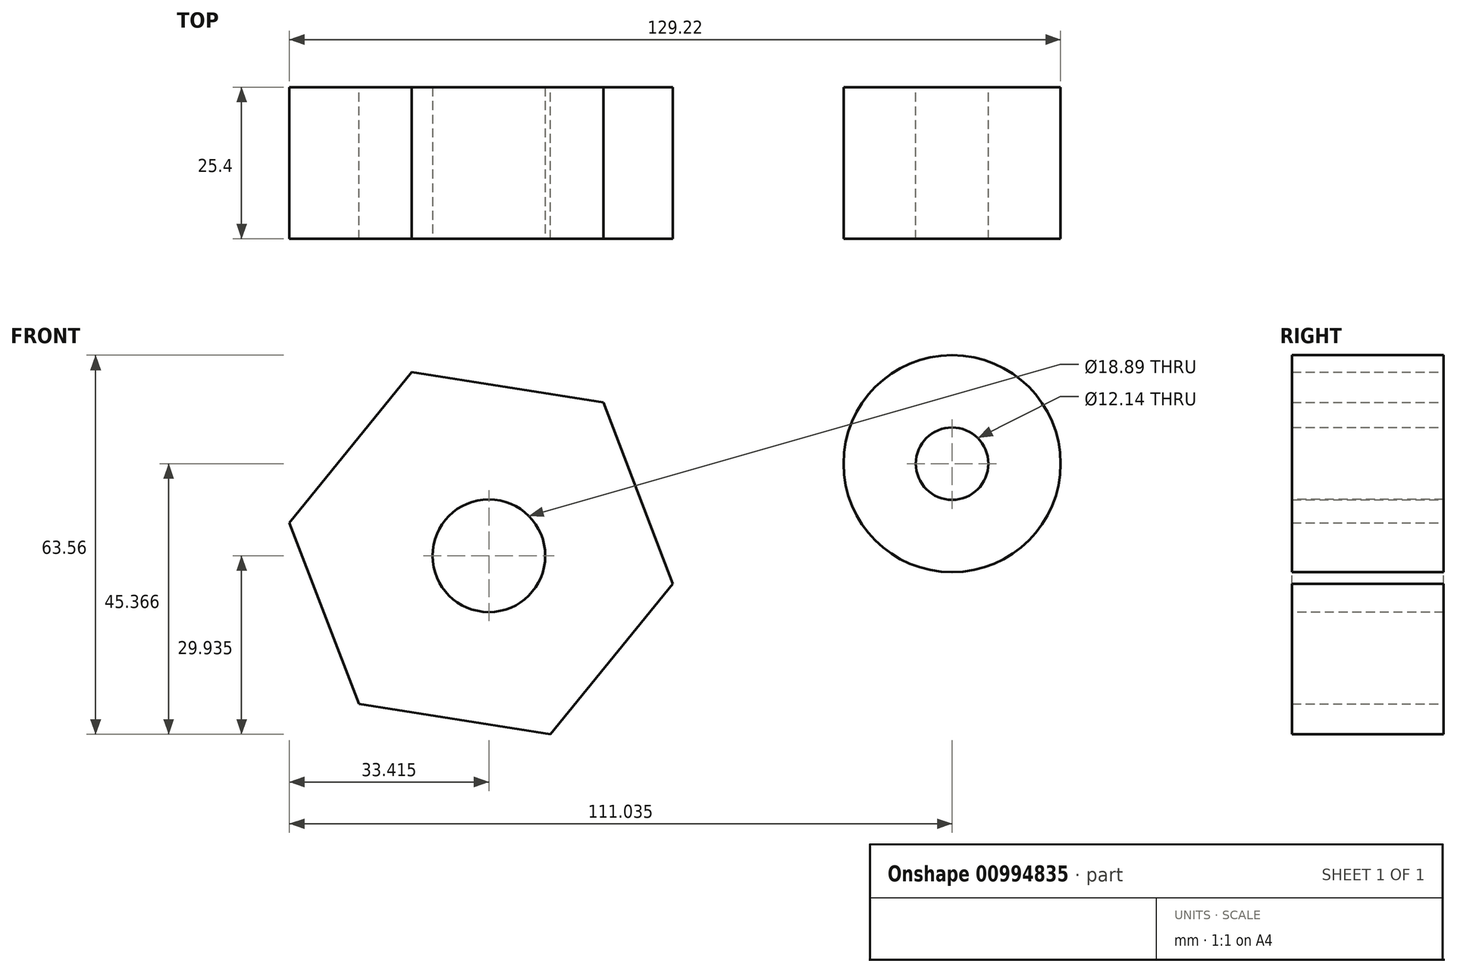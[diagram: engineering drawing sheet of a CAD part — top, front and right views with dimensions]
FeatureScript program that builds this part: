
annotation { "Feature Type Name" : "Feature", "Feature Type Description" : "" }
export const myFeature = defineFeature(function(context is Context, id is Id, definition is map)
    precondition{}
    {
        {
            var Q0;
            Q0=qCreatedBy(makeId("Front.planeOp"),FACE);
            var sketch = newSketch(context, id + "F0", { "sketchPlane" : qUnion([Q0])});
            skCircle(sketch, "E0", {"center": v(-46.4, -9.3) * mm, "radius": 16.6 * mm});
            skSolve(sketch);
        }
        {
            var Q0;
            Q0=qCreatedBy(makeId("Front.planeOp"),FACE);
            var sketch = newSketch(context, id + "F1", { "sketchPlane" : qUnion([Q0])});
            skCircle(sketch, "E1", {"center": v(46.81, -8.8) * mm, "radius": 18.19 * mm});
            skSolve(sketch);
        }
        {
            var Q0;
            Q0=makeQuery(id+"F0.imprint","IMPRINT",FACE,{"disambiguationData":[TD([[makeQuery(id+"F0.imprint","IMPRINT",EDGE,{"derivedFrom":sQuery(id+"F0.wireOp",EDGE,"E0")}),1.0]])]});
            extrude(context, id + "F2", {"entities" : qUnion([Q0]), "depth" : 25.4 * mm, "offsetDistance" : 25.4 * mm});
        }
        {
            var Q0;
            Q0=makeQuery(id+"F2.opExtrude","CAP_FACE",FACE,{"disambiguationData":[OSD([sQuery(id+"F0.wireOp",EDGE,"E0")])],"isStart":false});
            var sketch = newSketch(context, id + "F3", { "sketchPlane" : qUnion([Q0])});
            skCircle(sketch, "E2", {"center": v(-46.4, -9.3) * mm, "radius": 4.84 * mm});
            skSolve(sketch);
        }
        {
            var Q0;
            Q0 = qSketchRegion(id + "F3", true);
            var Q1;
            Q1=makeQuery(id+"F3.imprint","IMPRINT",FACE,{"disambiguationData":[TD([[makeQuery(id+"F3.imprint","IMPRINT",EDGE,{"derivedFrom":sQuery(id+"F3.wireOp",EDGE,"E2")}),1.0]])]});
            var Q2;
            Q2=makeQuery(id+"F3.imprint","IMPRINT",FACE,{"disambiguationData":[TD([[makeQuery(id+"F3.imprint","IMPRINT",EDGE,{"derivedFrom":sQuery(id+"F3.wireOp",EDGE,"E2")}),-1.0]])]});
            extrude(context, id + "F4", {"entities" : qUnion([Q0, Q1, Q2]), "operationType" : NewBodyOperationType.REMOVE, "oppositeDirection" : true, "depth" : 25.4 * mm, "offsetDistance" : 25.4 * mm});
        }
        {
            var Q0;
            Q0=makeQuery(id+"F1.imprint","IMPRINT",FACE,{"disambiguationData":[TD([[makeQuery(id+"F1.imprint","IMPRINT",EDGE,{"derivedFrom":sQuery(id+"F1.wireOp",EDGE,"E1")}),1.0]])]});
            extrude(context, id + "F5", {"entities" : qUnion([Q0]), "depth" : 25.4 * mm, "offsetDistance" : 25.4 * mm});
        }
        {
            var Q0;
            Q0=makeQuery(id+"F5.opExtrude","CAP_FACE",FACE,{"disambiguationData":[OSD([sQuery(id+"F1.wireOp",EDGE,"E1")])],"isStart":true});
            var sketch = newSketch(context, id + "F6", { "sketchPlane" : qUnion([Q0])});
            skCircle(sketch, "E3", {"center": v(-46.81, -8.8) * mm, "radius": 6.07 * mm});
            skSolve(sketch);
        }
        {
            var Q0;
            Q0=makeQuery(id+"F6.imprint","IMPRINT",FACE,{"disambiguationData":[TD([[makeQuery(id+"F6.imprint","IMPRINT",EDGE,{"derivedFrom":sQuery(id+"F6.wireOp",EDGE,"E3")}),1.0]])]});
            extrude(context, id + "F7", {"entities" : qUnion([Q0]), "operationType" : NewBodyOperationType.REMOVE, "oppositeDirection" : true, "depth" : 27.23 * mm, "offsetDistance" : 25.4 * mm});
        }
        {
            var Q0;
            Q0=qCreatedBy(makeId("Front.planeOp"),FACE);
            var sketch = newSketch(context, id + "F8", { "sketchPlane" : qUnion([Q0])});
            skCircle(sketch, "E4.cCircle", {"center": v(-32.11, -23.8) * mm, "radius": 32.51 * mm, "construction": true});
            skLineSegment(sketch, "E4.0", {"start": v(0, -28.91) * mm, "end": v(-20.48, -54.16) * mm});
            skLineSegment(sketch, "E4.1", {"start": v(-20.48, -54.16) * mm, "end": v(-52.6, -49.05) * mm});
            skLineSegment(sketch, "E4.2", {"start": v(-52.6, -49.05) * mm, "end": v(-64.22, -18.7) * mm});
            skLineSegment(sketch, "E4.3", {"start": v(-64.22, -18.7) * mm, "end": v(-43.74, 6.56) * mm});
            skLineSegment(sketch, "E4.4", {"start": v(-43.74, 6.56) * mm, "end": v(-11.63, 1.45) * mm});
            skLineSegment(sketch, "E4.5", {"start": v(-11.63, 1.45) * mm, "end": v(0, -28.91) * mm});
            skSolve(sketch);
        }
        {
            var Q0;
            Q0 = qSketchRegion(id + "F8", true);
            var Q1;
            Q1=makeQuery(id+"F8.imprint","IMPRINT",FACE,{"disambiguationData":[TD([[makeQuery(id+"F8.imprint","IMPRINT",EDGE,{"derivedFrom":sQuery(id+"F8.wireOp",EDGE,"E4.0")}),-1.0]])]});
            extrude(context, id + "F9", {"entities" : qUnion([Q0, Q1]), "depth" : 25.4 * mm, "offsetDistance" : 25.4 * mm});
        }
        {
            var Q0;
            Q0=makeQuery(id+"F9.opExtrude","CAP_FACE",FACE,{"disambiguationData":[OSD([sQuery(id+"F8.wireOp",EDGE,"E4.0"),sQuery(id+"F8.wireOp",EDGE,"E4.1"),sQuery(id+"F8.wireOp",EDGE,"E4.2"),sQuery(id+"F8.wireOp",EDGE,"E4.3"),sQuery(id+"F8.wireOp",EDGE,"E4.4"),sQuery(id+"F8.wireOp",EDGE,"E4.5")])],"isStart":false});
            var sketch = newSketch(context, id + "F10", { "sketchPlane" : qUnion([Q0])});
            skCircle(sketch, "E5", {"center": v(-30.8, -24.23) * mm, "radius": 9.45 * mm});
            skSolve(sketch);
        }
        {
            var Q0;
            Q0=makeQuery(id+"F10.imprint","IMPRINT",FACE,{"disambiguationData":[TD([[makeQuery(id+"F10.imprint","IMPRINT",EDGE,{"derivedFrom":sQuery(id+"F10.wireOp",EDGE,"E5")}),1.0]])]});
            extrude(context, id + "F11", {"entities" : qUnion([Q0]), "operationType" : NewBodyOperationType.REMOVE, "oppositeDirection" : true, "depth" : 25.4 * mm, "offsetDistance" : 25.4 * mm});
        }
    });
